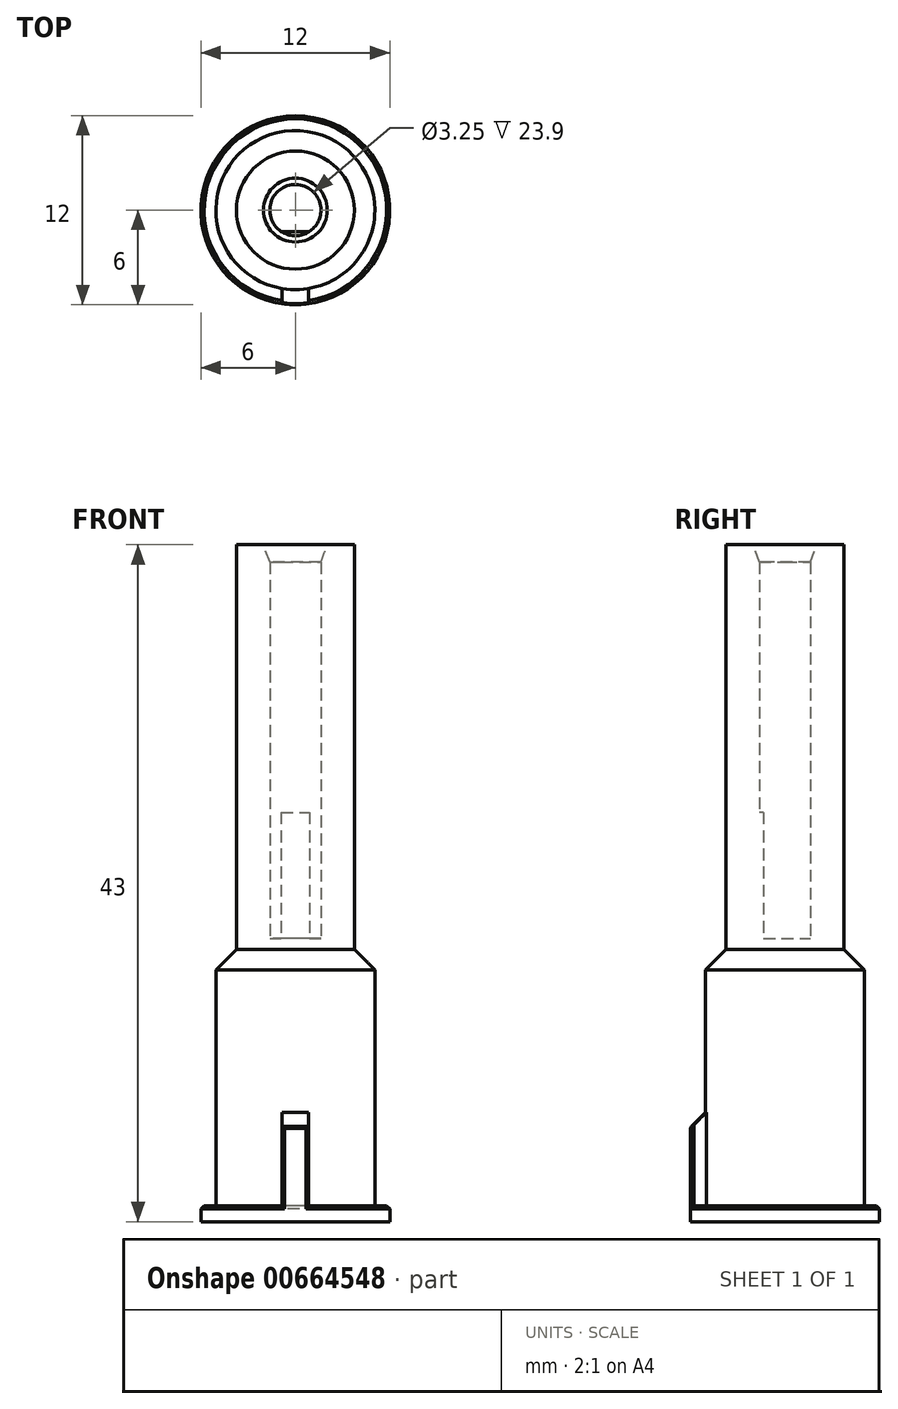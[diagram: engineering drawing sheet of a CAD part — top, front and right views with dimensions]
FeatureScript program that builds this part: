
annotation { "Feature Type Name" : "Feature", "Feature Type Description" : "" }
export const myFeature = defineFeature(function(context is Context, id is Id, definition is map)
    precondition{}
    {
        {
            var Q0;
            Q0=qCreatedBy(makeId("Top.planeOp"),FACE);
            var sketch = newSketch(context, id + "F0", { "sketchPlane" : qUnion([Q0])});
            skCircle(sketch, "E0", {"center": v(0, 0) * mm, "radius": 5.05 * mm});
            skCircle(sketch, "E1", {"center": v(0, 0) * mm, "radius": 1.63 * mm});
            skCircle(sketch, "E2", {"center": v(0, 0) * mm, "radius": 6 * mm});
            skLineSegment(sketch, "E3.bottom", {"start": v(0.9, -5.93) * mm, "end": v(-0.9, -5.93) * mm});
            skLineSegment(sketch, "E3.left", {"start": v(0.9, -5.93) * mm, "end": v(0.9, -4.97) * mm});
            skLineSegment(sketch, "E3.right", {"start": v(-0.9, -5.93) * mm, "end": v(-0.9, -4.97) * mm});
            skLineSegment(sketch, "E4", {"start": v(-0.9, -1.35) * mm, "end": v(0.9, -1.35) * mm});
            skPoint(sketch, "E3.top.end.orphan", {"position": v(-0.9, 5.93) * mm});
            skPoint(sketch, "E5.trimOffspring.end.orphan", {"position": v(0.9, 5.93) * mm});
            skCircle(sketch, "E6", {"center": v(0, 0) * mm, "radius": 3.75 * mm});
            skSolve(sketch);
        }
        {
            var Q0;
            {var subQ0=sQuery(id+"F0.wireOp",EDGE,"E3.left");Q0=makeQuery(id+"F0.imprint","IMPRINT",FACE,{"disambiguationData":[TD([[makeQuery(id+"F0.imprint","IMPRINT",EDGE,{"derivedFrom":subQ0}),-1.0]])]});}
            var Q1;
            Q1=makeQuery(id+"F0.imprint","IMPRINT",FACE,{"disambiguationData":[TD([[makeQuery(id+"F0.imprint","IMPRINT",EDGE,{"derivedFrom":sQuery(id+"F0.wireOp",EDGE,"E3.bottom")}),-1.0]])]});
            var Q2;
            {var subQ0=sQuery(id+"F0.wireOp",EDGE,"E3.bottom");Q2=makeQuery(id+"F0.imprint","IMPRINT",FACE,{"disambiguationData":[TD([[makeQuery(id+"F0.imprint","IMPRINT",EDGE,{"derivedFrom":subQ0}),1.0]])]});}
            extrude(context, id + "F1", {"entities" : qUnion([Q0, Q1, Q2]), "depth" : 1 * mm, "offsetDistance" : 25 * mm});
        }
        {
            var Q0;
            {var subQ0=sQuery(id+"F0.wireOp",EDGE,"E0");var subQ1=makeQuery(id+"F0.imprint","INTERSECT",VERTEX,{"derivedFrom":[subQ0,sQuery(id+"F0.wireOp",EDGE,"E3.left")]});Q0=makeQuery(id+"F0.imprint","IMPRINT",FACE,{"disambiguationData":[TD([[makeQuery(id+"F0.imprint","IMPRINT",EDGE,{"disambiguationData":[TD([[subQ1,1.0]])],"derivedFrom":subQ0}),1.0]])]});}
            var Q1;
            {var subQ0=sQuery(id+"F0.wireOp",EDGE,"E4");Q1=makeQuery(id+"F0.imprint","IMPRINT",FACE,{"disambiguationData":[TD([[makeQuery(id+"F0.imprint","IMPRINT",EDGE,{"derivedFrom":subQ0}),-1.0]])]});}
            var Q2;
            {var subQ0=sQuery(id+"F0.wireOp",EDGE,"E4");Q2=makeQuery(id+"F0.imprint","IMPRINT",FACE,{"disambiguationData":[TD([[makeQuery(id+"F0.imprint","IMPRINT",EDGE,{"derivedFrom":subQ0}),1.0]])]});}
            var Q3;
            Q3=makeQuery(id+"F0.imprint","IMPRINT",FACE,{"disambiguationData":[TD([[makeQuery(id+"F0.imprint","IMPRINT",EDGE,{"derivedFrom":sQuery(id+"F0.wireOp",EDGE,"E6")}),1.0]])]});
            extrude(context, id + "F2", {"entities" : qUnion([Q0, Q1, Q2, Q3]), "operationType" : NewBodyOperationType.ADD, "depth" : 16 * mm, "offsetDistance" : 25 * mm});
        }
        {
            var Q0;
            Q0=makeQuery(id+"F0.imprint","IMPRINT",FACE,{"disambiguationData":[TD([[makeQuery(id+"F0.imprint","IMPRINT",EDGE,{"derivedFrom":sQuery(id+"F0.wireOp",EDGE,"E6")}),1.0]])]});
            var Q1;
            {var subQ0=sQuery(id+"F0.wireOp",EDGE,"E4");Q1=makeQuery(id+"F0.imprint","IMPRINT",FACE,{"disambiguationData":[TD([[makeQuery(id+"F0.imprint","IMPRINT",EDGE,{"derivedFrom":subQ0}),1.0]])]});}
            var Q2;
            {var subQ0=sQuery(id+"F0.wireOp",EDGE,"E4");Q2=makeQuery(id+"F0.imprint","IMPRINT",FACE,{"disambiguationData":[TD([[makeQuery(id+"F0.imprint","IMPRINT",EDGE,{"derivedFrom":subQ0}),-1.0]])]});}
            var Q3;
            Q3=makeQuery(id+"F2.opExtrude","CAP_FACE",FACE,{"disambiguationData":[OSD([sQuery(id+"F0.wireOp",EDGE,"E0")])],"isStart":false});
            extrude(context, id + "F3", {"entities" : qUnion([Q0, Q1, Q2]), "operationType" : NewBodyOperationType.ADD, "endBound" : BoundingType.UP_TO_SURFACE, "depth" : 25 * mm, "endBoundEntityFace" : qUnion([Q3]), "hasOffset" : true, "offsetDistance" : 2 * mm, "offsetOppositeDirection" : true});
        }
        {
            var Q0;
            {var subQ0=sQuery(id+"F0.wireOp",EDGE,"E4");Q0=makeQuery(id+"F0.imprint","IMPRINT",FACE,{"disambiguationData":[TD([[makeQuery(id+"F0.imprint","IMPRINT",EDGE,{"derivedFrom":subQ0}),-1.0]])]});}
            var Q1;
            Q1=makeQuery(id+"F0.imprint","IMPRINT",FACE,{"disambiguationData":[TD([[makeQuery(id+"F0.imprint","IMPRINT",EDGE,{"derivedFrom":sQuery(id+"F0.wireOp",EDGE,"E6")}),1.0]])]});
            var Q2;
            Q2=makeQuery(id+"F3.opExtrude","CAP_FACE",FACE,{"disambiguationData":[OSD([sQuery(id+"F0.wireOp",EDGE,"E6")])],"isStart":false});
            extrude(context, id + "F4", {"entities" : qUnion([Q0, Q1]), "operationType" : NewBodyOperationType.ADD, "endBound" : BoundingType.UP_TO_SURFACE, "depth" : 25 * mm, "endBoundEntityFace" : qUnion([Q2]), "hasOffset" : true, "offsetDistance" : 8 * mm, "offsetOppositeDirection" : true});
        }
        {
            var Q0;
            Q0=makeQuery(id+"F0.imprint","IMPRINT",FACE,{"disambiguationData":[TD([[makeQuery(id+"F0.imprint","IMPRINT",EDGE,{"derivedFrom":sQuery(id+"F0.wireOp",EDGE,"E6")}),1.0]])]});
            var Q1;
            Q1=makeQuery(id+"F4.opExtrude","CAP_FACE",FACE,{"disambiguationData":[OSD([sQuery(id+"F0.wireOp",EDGE,"E1"),sQuery(id+"F0.wireOp",EDGE,"E4"),sQuery(id+"F0.wireOp",EDGE,"E6")])],"isStart":false});
            extrude(context, id + "F5", {"entities" : qUnion([Q0]), "operationType" : NewBodyOperationType.ADD, "endBound" : BoundingType.UP_TO_SURFACE, "depth" : 25 * mm, "endBoundEntityFace" : qUnion([Q1]), "hasOffset" : true, "offsetDistance" : 17 * mm, "offsetOppositeDirection" : true});
        }
        {
            var Q0;
            Q0=qCreatedBy(makeId("Front.planeOp"),FACE);
            var sketch = newSketch(context, id + "F6", { "sketchPlane" : qUnion([Q0])});
            skLineSegment(sketch, "E7.bottom", {"start": v(0.85, 7) * mm, "end": v(-0.85, 7) * mm});
            skLineSegment(sketch, "E7.top", {"start": v(0.85, 1) * mm, "end": v(-0.85, 1) * mm});
            skLineSegment(sketch, "E7.left", {"start": v(0.85, 7) * mm, "end": v(0.85, 1) * mm});
            skLineSegment(sketch, "E7.right", {"start": v(-0.85, 7) * mm, "end": v(-0.85, 1) * mm});
            skPoint(sketch, "E7.middle", {"position": v(0, 4) * mm});
            skSolve(sketch);
        }
        {
            var Q0;
            Q0 = qSketchRegion(id + "F6", true);
            var Q1;
            Q1=makeQuery(id+"F1.opExtrude","SWEPT_FACE",FACE,{"disambiguationData":[OSD([sQuery(id+"F0.wireOp",EDGE,"E2")])]});
            extrude(context, id + "F7", {"entities" : qUnion([Q0]), "operationType" : NewBodyOperationType.ADD, "endBound" : BoundingType.UP_TO_SURFACE, "depth" : 6 * mm, "endBoundEntityFace" : qUnion([Q1]), "offsetDistance" : 25 * mm});
        }
        {
            var Q0;
            Q0=makeQuery(id+"F7.opExtrude","CAP_EDGE",EDGE,{"disambiguationData":[OSD([sQuery(id+"F6.wireOp",EDGE,"E7.bottom")])],"isStart":false});
            chamfer(context, id + "F8", {"entities" : qUnion([Q0]), "width" : 1 * mm, "tangentPropagation" : true});
        }
        {
            var Q0;
            Q0=makeQuery(id+"F7.opExtrude","CAP_EDGE",EDGE,{"disambiguationData":[OSD([sQuery(id+"F6.wireOp",EDGE,"E7.right")])],"isStart":false});
            var Q1;
            Q1=makeQuery(id+"F7.opExtrude","CAP_EDGE",EDGE,{"disambiguationData":[OSD([sQuery(id+"F6.wireOp",EDGE,"E7.left")])],"isStart":false});
            var Q2;
            {var subQ0=sQuery(id+"F6.wireOp",EDGE,"E7.bottom");Q2=makeQuery(id+"F8.opChamfer","BLEND_EDGE",EDGE,{"blendedFrom":[makeQuery(id+"F7.opExtrude","CAP_EDGE",EDGE,{"disambiguationData":[OSD([subQ0])],"isStart":false}),makeQuery(id+"F7.boolean.opBoolean","MERGE",FACE,{"derivedFrom":[makeQuery(id+"F1.opExtrude","SWEPT_FACE",FACE,{"disambiguationData":[OSD([sQuery(id+"F0.wireOp",EDGE,"E2")])]}),makeQuery(id+"F7.opExtrude","CAP_FACE",FACE,{"disambiguationData":[OSD([subQ0,sQuery(id+"F6.wireOp",EDGE,"E7.top"),sQuery(id+"F6.wireOp",EDGE,"E7.left"),sQuery(id+"F6.wireOp",EDGE,"E7.right")])],"isStart":false})]})],"blendedInto":[makeQuery(id+"F7.boolean.opBoolean","MERGE",FACE,{"derivedFrom":[makeQuery(id+"F1.opExtrude","SWEPT_FACE",FACE,{"disambiguationData":[OSD([sQuery(id+"F0.wireOp",EDGE,"E2")])]}),makeQuery(id+"F7.opExtrude","CAP_FACE",FACE,{"disambiguationData":[OSD([subQ0,sQuery(id+"F6.wireOp",EDGE,"E7.top"),sQuery(id+"F6.wireOp",EDGE,"E7.left"),sQuery(id+"F6.wireOp",EDGE,"E7.right")])],"isStart":false})]})]});}
            var Q3;
            Q3=makeQuery(id+"F1.opExtrude","CAP_EDGE",EDGE,{"disambiguationData":[OSD([sQuery(id+"F0.wireOp",EDGE,"E2")])],"isStart":false});
            chamfer(context, id + "F9", {"entities" : qUnion([Q0, Q1, Q2, Q3]), "width" : 0.2 * mm, "tangentPropagation" : true});
        }
        {
            var Q0;
            Q0=makeQuery(id+"F5.opExtrude","CAP_EDGE",EDGE,{"disambiguationData":[OSD([sQuery(id+"F0.wireOp",EDGE,"E1")])],"isStart":false});
            chamfer(context, id + "F10", {"entities" : qUnion([Q0]), "chamferType" : ChamferType.TWO_OFFSETS, "width1" : 1.1 * mm, "oppositeDirection" : false, "width2" : 0.4 * mm, "tangentPropagation" : true});
        }
        {
            var Q0;
            Q0=makeQuery(id+"F3.boolean.opBoolean","INTERSECT",EDGE,{"derivedFrom":[makeQuery(id+"F2.opExtrude","CAP_FACE",FACE,{"disambiguationData":[OSD([sQuery(id+"F0.wireOp",EDGE,"E0")])],"isStart":false}),makeQuery(id+"F3.opExtrude","SWEPT_FACE",FACE,{"disambiguationData":[OSD([sQuery(id+"F0.wireOp",EDGE,"E6")])]})]});
            chamfer(context, id + "F11", {"entities" : qUnion([Q0]), "width" : 1.3 * mm, "tangentPropagation" : true});
        }
    });
